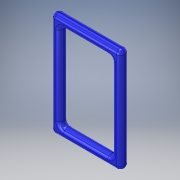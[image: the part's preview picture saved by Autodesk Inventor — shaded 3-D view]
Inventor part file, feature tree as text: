
AUTODESK INVENTOR PART (.ipt)
format: ipt  version: 2019.4 (Build 234330000, 330)  size: 165,376 bytes
history: native  units: mm
features: extrude x1, fillet x1, sketch x1
ambient origin geometry x8: Origin, YZ Plane, XZ Plane, XY Plane, X Axis, Y Axis, Z Axis, Center Point
bodies: Solid1 (feature_tree)
feature tree (3):
  extrude  "Extrusion1"  Depth=10.0mm
  fillet  "Fillet1"  Radius=1.0mm
  sketch  "Sketch1"  dims[d0=6.0mm d1=10.0mm d2=1.0mm d3=1.0mm d4=0.0mm d5=0.45mm]
